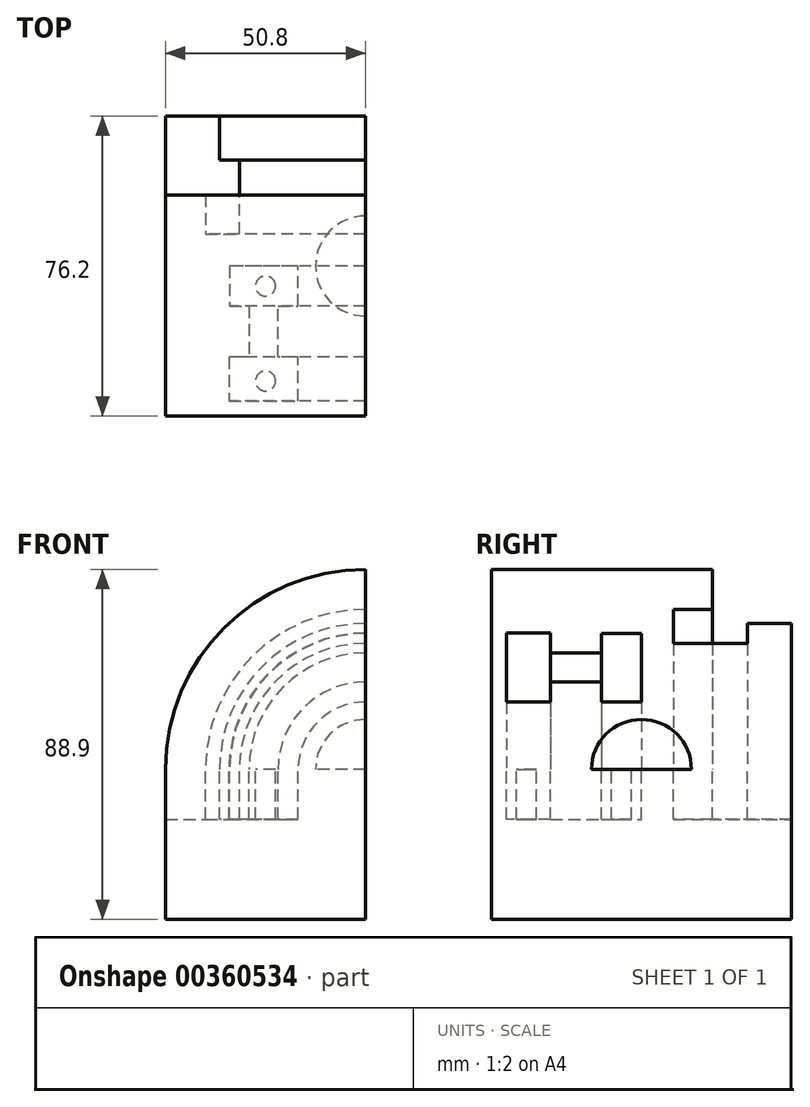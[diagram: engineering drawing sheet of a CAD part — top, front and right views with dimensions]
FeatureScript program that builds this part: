
annotation { "Feature Type Name" : "Feature", "Feature Type Description" : "" }
export const myFeature = defineFeature(function(context is Context, id is Id, definition is map)
    precondition{}
    {
        {
            var Q0;
            Q0=qCreatedBy(makeId("Top.planeOp"),FACE);
            var sketch = newSketch(context, id + "F0", { "sketchPlane" : qUnion([Q0])});
            skLineSegment(sketch, "E0.bottom", {"start": v(-25.4, 38.1) * mm, "end": v(25.4, 38.1) * mm});
            skLineSegment(sketch, "E0.top", {"start": v(-25.4, -38.1) * mm, "end": v(25.4, -38.1) * mm});
            skLineSegment(sketch, "E0.left", {"start": v(-25.4, 38.1) * mm, "end": v(-25.4, -38.1) * mm});
            skLineSegment(sketch, "E0.right", {"start": v(25.4, 38.1) * mm, "end": v(25.4, -38.1) * mm});
            skSolve(sketch);
        }
        {
            var Q0;
            Q0=makeQuery(id+"F0.imprint","IMPRINT",FACE,{"disambiguationData":[TD([[makeQuery(id+"F0.imprint","IMPRINT",EDGE,{"derivedFrom":sQuery(id+"F0.wireOp",EDGE,"E0.bottom")}),-1.0]])]});
            extrude(context, id + "F1", {"entities" : qUnion([Q0]), "depth" : 38.1 * mm});
        }
        {
            var Q0;
            Q0=makeQuery(id+"F1.opExtrude","CAP_FACE",FACE,{"disambiguationData":[OSD([sQuery(id+"F0.wireOp",EDGE,"E0.bottom"),sQuery(id+"F0.wireOp",EDGE,"E0.top"),sQuery(id+"F0.wireOp",EDGE,"E0.left"),sQuery(id+"F0.wireOp",EDGE,"E0.right")])],"isStart":false});
            var sketch = newSketch(context, id + "F2", { "sketchPlane" : qUnion([Q0])});
            skLineSegment(sketch, "E1", {"start": v(-25.4, 38.1) * mm, "end": v(-25.4, 18.03) * mm});
            skLineSegment(sketch, "E2", {"start": v(-25.4, 18.03) * mm, "end": v(-15.24, 18.03) * mm});
            skLineSegment(sketch, "E3", {"start": v(-15.24, 18.03) * mm, "end": v(-15.24, 8.18) * mm});
            skLineSegment(sketch, "E4", {"start": v(-15.24, 8.18) * mm, "end": v(-6.6, 8.18) * mm});
            skLineSegment(sketch, "E5", {"start": v(-6.6, 8.18) * mm, "end": v(-6.6, 26.98) * mm});
            skLineSegment(sketch, "E6", {"start": v(-6.6, 26.98) * mm, "end": v(-11.68, 26.98) * mm});
            skLineSegment(sketch, "E7", {"start": v(-11.68, 26.98) * mm, "end": v(-11.68, 38.1) * mm});
            skLineSegment(sketch, "E8", {"start": v(-11.68, 38.1) * mm, "end": v(-25.4, 38.1) * mm});
            skArc(sketch, "E9", {"start": v(25.4, -12.7) * mm, "mid": v(12.7, 0) * mm, "end": v(25.4, 12.7) * mm});
            skLineSegment(sketch, "E10", {"start": v(-9.27, -34.29) * mm, "end": v(8.25, -34.29) * mm});
            skLineSegment(sketch, "E11", {"start": v(8.25, -34.29) * mm, "end": v(8.25, -23.11) * mm});
            skLineSegment(sketch, "E12", {"start": v(8.25, -23.11) * mm, "end": v(3.17, -23.11) * mm});
            skLineSegment(sketch, "E13", {"start": v(3.17, -23.11) * mm, "end": v(3.17, -10.16) * mm});
            skLineSegment(sketch, "E14", {"start": v(3.17, -10.16) * mm, "end": v(8.26, -10.16) * mm});
            skLineSegment(sketch, "E15", {"start": v(8.26, -10.16) * mm, "end": v(8.26, 0) * mm});
            skLineSegment(sketch, "E16", {"start": v(8.26, 0) * mm, "end": v(-9.12, 0) * mm});
            skLineSegment(sketch, "E17", {"start": v(-9.12, 0) * mm, "end": v(-9.12, -10.16) * mm});
            skLineSegment(sketch, "E18", {"start": v(-9.12, -10.16) * mm, "end": v(-4.2, -10.16) * mm});
            skLineSegment(sketch, "E19", {"start": v(-4.2, -10.16) * mm, "end": v(-4.2, -23.11) * mm});
            skLineSegment(sketch, "E20", {"start": v(-4.2, -23.11) * mm, "end": v(-9.27, -23.11) * mm});
            skLineSegment(sketch, "E21", {"start": v(-9.27, -23.11) * mm, "end": v(-9.27, -34.29) * mm});
            skCircle(sketch, "E22", {"center": v(0, -29.2) * mm, "radius": 2.54 * mm});
            skCircle(sketch, "E23", {"center": v(0, -5.08) * mm, "radius": 2.54 * mm});
            skLineSegment(sketch, "E24.0.0", {"start": v(-25.4, 38.1) * mm, "end": v(-25.4, -38.1) * mm});
            skLineSegment(sketch, "E24.0.1", {"start": v(-25.4, -38.1) * mm, "end": v(25.4, -38.1) * mm});
            skLineSegment(sketch, "E24.0.2", {"start": v(25.4, -38.1) * mm, "end": v(25.4, 38.1) * mm});
            skLineSegment(sketch, "E24.0.3", {"start": v(25.4, 38.1) * mm, "end": v(-25.4, 38.1) * mm});
            skSolve(sketch);
        }
        {
            var Q0;
            {var subQ0=sQuery(id+"F2.wireOp",EDGE,"E9");var subQ1=makeQuery(id+"F1.opExtrude","CAP_EDGE",EDGE,{"disambiguationData":[OSD([sQuery(id+"F0.wireOp",EDGE,"E0.right")])],"isStart":false});var subQ2=makeQuery(id+"F2.imprint","INTERSECT",VERTEX,{"disambiguationData":[OD(0.0)],"derivedFrom":[subQ1,subQ0]});Q0=makeQuery(id+"F2.imprint","IMPRINT",FACE,{"disambiguationData":[TD([[makeQuery(id+"F2.imprint","IMPRINT",EDGE,{"disambiguationData":[TD([[subQ2,-1.0]])],"derivedFrom":subQ0}),-1.0]])]});}
            var Q1;
            {var subQ0=sQuery(id+"F2.wireOp",EDGE,"E9");var subQ1=makeQuery(id+"F1.opExtrude","CAP_EDGE",EDGE,{"disambiguationData":[OSD([sQuery(id+"F0.wireOp",EDGE,"E0.right")])],"isStart":false});var subQ2=makeQuery(id+"F2.imprint","INTERSECT",VERTEX,{"disambiguationData":[OD(1.0)],"derivedFrom":[subQ1,subQ0]});Q1=makeQuery(id+"F2.imprint","IMPRINT",FACE,{"disambiguationData":[TD([[makeQuery(id+"F2.imprint","IMPRINT",EDGE,{"disambiguationData":[TD([[subQ2,1.0]])],"derivedFrom":subQ0}),-1.0]])]});}
            var Q2;
            Q2=makeQuery(id+"F1.opExtrude","CAP_EDGE",EDGE,{"disambiguationData":[OSD([sQuery(id+"F0.wireOp",EDGE,"E0.right")])],"isStart":false});
            revolve(context, id + "F3", {"operationType" : NewBodyOperationType.ADD, "entities" : qUnion([Q0, Q1]), "axis" : qUnion([Q2]), "revolveType" : RevolveType.ONE_DIRECTION, "oppositeDirection" : true, "angle" : 90 * degree});
        }
        {
            var Q0;
            {var subQ0=sQuery(id+"F2.wireOp",EDGE,"E2");Q0=makeQuery(id+"F2.imprint","IMPRINT",FACE,{"disambiguationData":[TD([[makeQuery(id+"F2.imprint","IMPRINT",EDGE,{"derivedFrom":subQ0}),1.0]])]});}
            extrude(context, id + "F4", {"entities" : qUnion([Q0]), "operationType" : NewBodyOperationType.REMOVE, "oppositeDirection" : true, "depth" : 12.7 * mm});
        }
        {
            var Q0;
            {var subQ5=sQuery(id+"F2.wireOp",EDGE,"E21");var subQ6=sQuery(id+"F2.wireOp",EDGE,"E10");var subQ7=makeQuery(id+"F2.imprint","INTERSECT",VERTEX,{"derivedFrom":[subQ6,subQ5]});Q0=makeQuery(id+"F2.imprint","IMPRINT",FACE,{"disambiguationData":[TD([[makeQuery(id+"F2.imprint","IMPRINT",EDGE,{"disambiguationData":[TD([[subQ7,-1.0]])],"derivedFrom":subQ6}),1.0]])]});}
            var Q1;
            {var subQ17=sQuery(id+"F2.wireOp",EDGE,"E18");Q1=makeQuery(id+"F2.imprint","IMPRINT",FACE,{"disambiguationData":[TD([[makeQuery(id+"F2.imprint","IMPRINT",EDGE,{"derivedFrom":subQ17}),1.0]])]});}
            var Q2;
            {var subQ18=sQuery(id+"F2.wireOp",EDGE,"E12");Q2=makeQuery(id+"F2.imprint","IMPRINT",FACE,{"disambiguationData":[TD([[makeQuery(id+"F2.imprint","IMPRINT",EDGE,{"derivedFrom":subQ18}),1.0]])]});}
            var Q3;
            {var subQ5=sQuery(id+"F2.wireOp",EDGE,"E11");var subQ7=sQuery(id+"F2.wireOp",EDGE,"E10");var subQ8=makeQuery(id+"F2.imprint","INTERSECT",VERTEX,{"derivedFrom":[subQ7,subQ5]});Q3=makeQuery(id+"F2.imprint","IMPRINT",FACE,{"disambiguationData":[TD([[makeQuery(id+"F2.imprint","IMPRINT",EDGE,{"disambiguationData":[TD([[subQ8,1.0]])],"derivedFrom":subQ7}),1.0]])]});}
            extrude(context, id + "F5", {"entities" : qUnion([Q0, Q1, Q2, Q3]), "operationType" : NewBodyOperationType.REMOVE, "oppositeDirection" : true, "depth" : 12.7 * mm});
        }
    });
